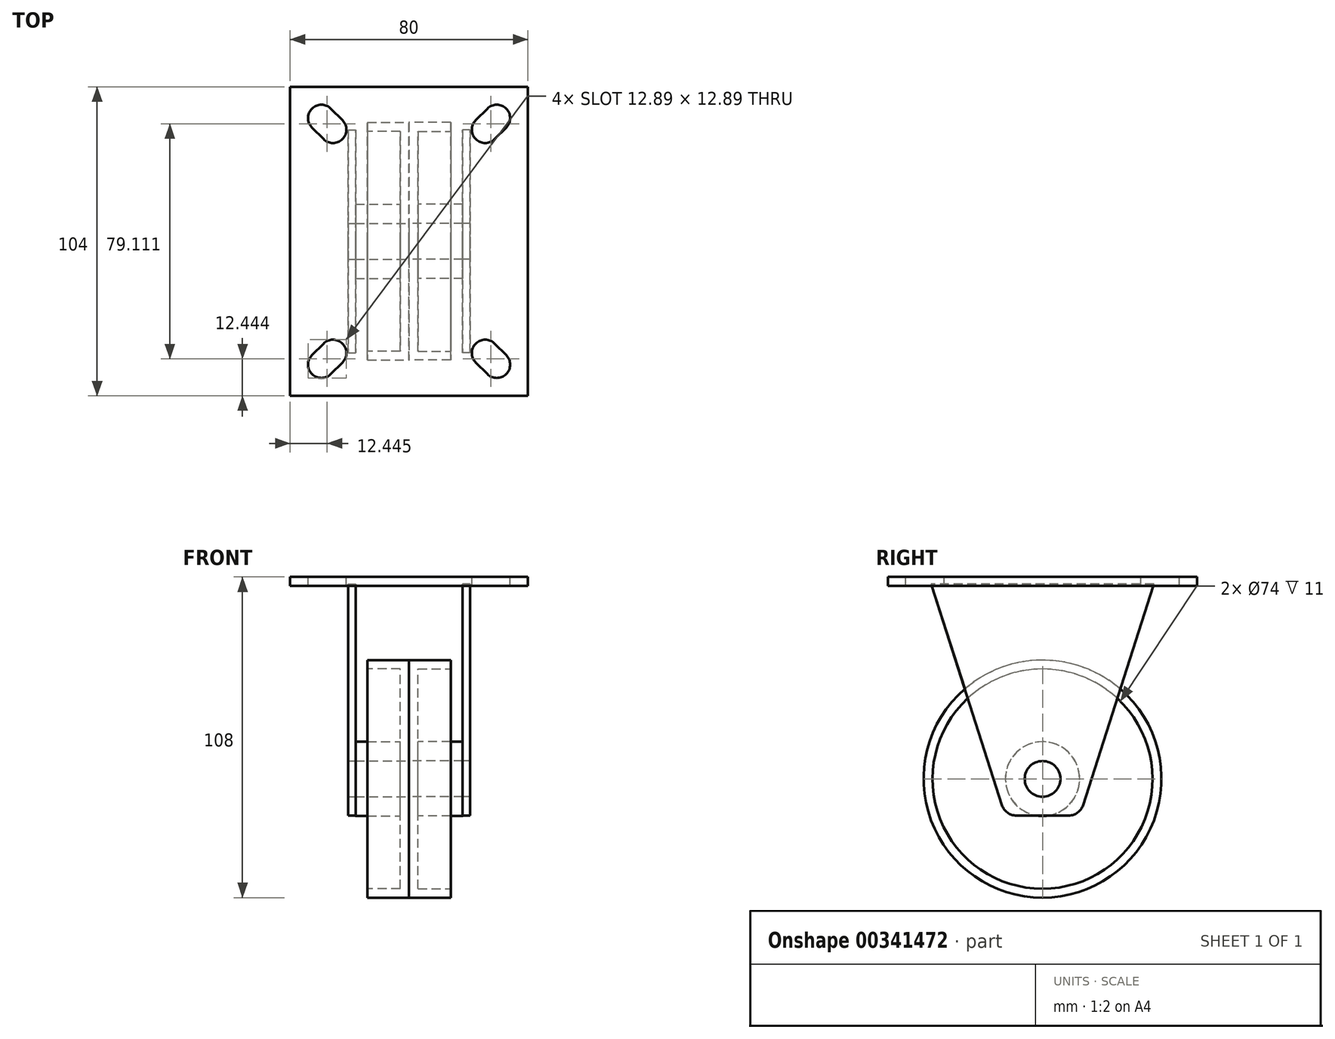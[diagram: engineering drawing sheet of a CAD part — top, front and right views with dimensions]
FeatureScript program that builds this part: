
annotation { "Feature Type Name" : "Feature", "Feature Type Description" : "" }
export const myFeature = defineFeature(function(context is Context, id is Id, definition is map)
    precondition{}
    {
        {
            var Q0;
            Q0=qCreatedBy(makeId("Front.planeOp"),FACE);
            var sketch = newSketch(context, id + "F0", { "sketchPlane" : qUnion([Q0])});
            skLineSegment(sketch, "E0.bottom", {"start": v(-49.77, 0) * mm, "end": v(53.7, 0) * mm, "construction": true});
            skLineSegment(sketch, "E0.top", {"start": v(-49.77, -108) * mm, "end": v(53.7, -108) * mm, "construction": true});
            skLineSegment(sketch, "E0.left", {"start": v(-49.77, 0) * mm, "end": v(-49.77, -108) * mm, "construction": true});
            skLineSegment(sketch, "E0.right", {"start": v(53.7, 0) * mm, "end": v(53.7, -108) * mm, "construction": true});
            skSolve(sketch);
        }
        {
            var Q0;
            Q0=qCreatedBy(makeId("Top.planeOp"),FACE);
            var sketch = newSketch(context, id + "F1", { "sketchPlane" : qUnion([Q0])});
            skLineSegment(sketch, "E1.bottom", {"start": v(-40, 52) * mm, "end": v(40, 52) * mm});
            skLineSegment(sketch, "E1.top", {"start": v(-40, -52) * mm, "end": v(40, -52) * mm});
            skLineSegment(sketch, "E1.left", {"start": v(-40, 52) * mm, "end": v(-40, -52) * mm});
            skLineSegment(sketch, "E1.right", {"start": v(40, 52) * mm, "end": v(40, -52) * mm});
            skLineSegment(sketch, "E2", {"start": v(0, 52) * mm, "end": v(0, -52) * mm, "construction": true});
            skLineSegment(sketch, "E3", {"start": v(-40, 0) * mm, "end": v(0, 0) * mm, "construction": true});
            skLineSegment(sketch, "E4", {"start": v(0, 0) * mm, "end": v(40, 0) * mm, "construction": true});
            skArc(sketch, "E5", {"start": v(-26.32, 44.68) * mm, "mid": v(-32.68, 44.68) * mm, "end": v(-32.68, 38.32) * mm});
            skLineSegment(sketch, "E6", {"start": v(-29.5, 41.5) * mm, "end": v(-26.32, 44.68) * mm, "construction": true});
            skLineSegment(sketch, "E7", {"start": v(-26.32, 44.68) * mm, "end": v(-22.43, 40.8) * mm});
            skLineSegment(sketch, "E8", {"start": v(-22.43, 40.8) * mm, "end": v(-28.8, 34.43) * mm, "construction": true});
            skLineSegment(sketch, "E9", {"start": v(-28.8, 34.43) * mm, "end": v(-32.68, 38.32) * mm});
            skLineSegment(sketch, "E10", {"start": v(-32.68, 38.32) * mm, "end": v(-29.5, 41.5) * mm, "construction": true});
            skLineSegment(sketch, "E11", {"start": v(-29.5, 41.5) * mm, "end": v(-25, 41.5) * mm, "construction": true});
            skArc(sketch, "E12", {"start": v(-28.8, 34.43) * mm, "mid": v(-22.43, 34.43) * mm, "end": v(-22.43, 40.8) * mm});
            skLineSegment(sketch, "E13.MirrorCS", {"start": v(28.8, 34.43) * mm, "end": v(32.68, 38.32) * mm});
            skArc(sketch, "E14.MirrorCS", {"start": v(26.32, 44.68) * mm, "mid": v(32.68, 44.68) * mm, "end": v(32.68, 38.32) * mm});
            skLineSegment(sketch, "E15.MirrorCS", {"start": v(26.32, 44.68) * mm, "end": v(22.43, 40.8) * mm});
            skArc(sketch, "E16.MirrorCS", {"start": v(28.8, 34.43) * mm, "mid": v(22.43, 34.43) * mm, "end": v(22.43, 40.8) * mm});
            skLineSegment(sketch, "E17.MirrorCS", {"start": v(-28.8, -34.43) * mm, "end": v(-32.68, -38.32) * mm});
            skArc(sketch, "E18.MirrorCS", {"start": v(-28.8, -34.43) * mm, "mid": v(-22.43, -34.43) * mm, "end": v(-22.43, -40.8) * mm});
            skLineSegment(sketch, "E19.MirrorCS", {"start": v(-26.32, -44.68) * mm, "end": v(-22.43, -40.8) * mm});
            skArc(sketch, "E20.MirrorCS", {"start": v(-26.32, -44.68) * mm, "mid": v(-32.68, -44.68) * mm, "end": v(-32.68, -38.32) * mm});
            skArc(sketch, "E21.MirrorCS", {"start": v(26.32, -44.68) * mm, "mid": v(32.68, -44.68) * mm, "end": v(32.68, -38.32) * mm});
            skArc(sketch, "E22.MirrorCS", {"start": v(28.8, -34.43) * mm, "mid": v(22.43, -34.43) * mm, "end": v(22.43, -40.8) * mm});
            skLineSegment(sketch, "E23.MirrorCS", {"start": v(26.32, -44.68) * mm, "end": v(22.43, -40.8) * mm});
            skLineSegment(sketch, "E24.MirrorCS", {"start": v(28.8, -34.43) * mm, "end": v(32.68, -38.32) * mm});
            skLineSegment(sketch, "E25", {"start": v(-30.74, 36.37) * mm, "end": v(-24.37, 42.74) * mm, "construction": true});
            skLineSegment(sketch, "E26", {"start": v(-25.61, 37.61) * mm, "end": v(-29.5, 41.5) * mm, "construction": true});
            skLineSegment(sketch, "E27", {"start": v(-27.56, 39.56) * mm, "end": v(0, 39.56) * mm, "construction": true});
            skLineSegment(sketch, "E28", {"start": v(-27.56, 39.56) * mm, "end": v(-27.56, 52) * mm, "construction": true});
            skLineSegment(sketch, "E29", {"start": v(-27.56, 39.56) * mm, "end": v(-27.56, 0) * mm, "construction": true});
            skSolve(sketch);
        }
        {
            var Q0;
            Q0=makeQuery(id+"F1.imprint","IMPRINT",FACE,{"disambiguationData":[TD([[makeQuery(id+"F1.imprint","IMPRINT",EDGE,{"derivedFrom":sQuery(id+"F1.wireOp",EDGE,"E1.bottom")}),-1.0]])]});
            extrude(context, id + "F2", {"entities" : qUnion([Q0]), "oppositeDirection" : true, "depth" : 3 * mm});
        }
        {
            var Q0;
            Q0=qCreatedBy(makeId("Right.planeOp"),FACE);
            var sketch = newSketch(context, id + "F3", { "sketchPlane" : qUnion([Q0])});
            skCircle(sketch, "E30", {"center": v(0, -68) * mm, "radius": 40 * mm});
            skLineSegment(sketch, "E31", {"start": v(17.4, -108) * mm, "end": v(-52.03, -108) * mm, "construction": true});
            skCircle(sketch, "E32", {"center": v(0, -68) * mm, "radius": 6 * mm});
            skCircle(sketch, "E33", {"center": v(0, -68) * mm, "radius": 12.5 * mm});
            skSolve(sketch);
        }
        {
            var Q0;
            Q0=makeQuery(id+"F3.imprint","IMPRINT",FACE,{"disambiguationData":[TD([[makeQuery(id+"F3.imprint","IMPRINT",EDGE,{"derivedFrom":sQuery(id+"F3.wireOp",EDGE,"E30")}),1.0]])]});
            extrude(context, id + "F4", {"entities" : qUnion([Q0]), "depth" : 28 / 2 * mm});
        }
        {
            var Q0;
            Q0=makeQuery(id+"F4.opExtrude","CAP_FACE",FACE,{"disambiguationData":[OSD([sQuery(id+"F3.wireOp",EDGE,"E30")])],"isStart":false});
            var sketch = newSketch(context, id + "F5", { "sketchPlane" : qUnion([Q0])});
            skCircle(sketch, "E34", {"center": v(0, -68) * mm, "radius": 37 * mm});
            skSolve(sketch);
        }
        {
            var Q0;
            Q0=makeQuery(id+"F5.imprint","IMPRINT",FACE,{"disambiguationData":[TD([[makeQuery(id+"F5.imprint","IMPRINT",EDGE,{"derivedFrom":sQuery(id+"F5.wireOp",EDGE,"E34")}),1.0]])]});
            extrude(context, id + "F6", {"entities" : qUnion([Q0]), "operationType" : NewBodyOperationType.REMOVE, "oppositeDirection" : true, "depth" : (28 / 2 - 3) * mm});
        }
        {
            var Q0;
            Q0=makeQuery(id+"F3.imprint","IMPRINT",FACE,{"disambiguationData":[TD([[makeQuery(id+"F3.imprint","IMPRINT",EDGE,{"derivedFrom":sQuery(id+"F3.wireOp",EDGE,"E32")}),-1.0]])]});
            extrude(context, id + "F7", {"entities" : qUnion([Q0]), "operationType" : NewBodyOperationType.ADD, "depth" : 36 / 2 * mm});
        }
        {
            var Q0;
            Q0=makeQuery(id+"F4.opExtrude","SWEPT_BODY",BODY,{"disambiguationData":[OSD([sQuery(id+"F3.wireOp",EDGE,"E30")])]});
            var Q1;
            Q1=qCreatedBy(makeId("Right.planeOp"),FACE);
            mirror(context, id + "F8", {"operationType" : NewBodyOperationType.ADD, "entities" : qUnion([Q0]), "mirrorPlane" : qUnion([Q1])});
        }
        {
            var Q0;
            Q0=makeQuery(id+"F7.opExtrude","CAP_FACE",FACE,{"disambiguationData":[OSD([sQuery(id+"F3.wireOp",EDGE,"E32"),sQuery(id+"F3.wireOp",EDGE,"E33")])],"isStart":false});
            var sketch = newSketch(context, id + "F9", { "sketchPlane" : qUnion([Q0])});
            skLineSegment(sketch, "E35", {"start": v(-8.85, -80.35) * mm, "end": v(8.85, -80.35) * mm});
            skLineSegment(sketch, "E36", {"start": v(13.61, -76.88) * mm, "end": v(37.5, -2.4) * mm});
            skLineSegment(sketch, "E37", {"start": v(37.5, -2.4) * mm, "end": v(-37.5, -2.4) * mm});
            skLineSegment(sketch, "E38", {"start": v(-37.5, -2.4) * mm, "end": v(-13.61, -76.88) * mm});
            skPoint(sketch, "E39.visualSharp", {"position": v(-12.5, -80.35) * mm});
            skArc(sketch, "E39.filletArc", {"start": v(-13.61, -76.88) * mm, "mid": v(-11.8, -79.4) * mm, "end": v(-8.85, -80.35) * mm});
            skPoint(sketch, "E40.visualSharp", {"position": v(12.5, -80.35) * mm});
            skArc(sketch, "E40.filletArc", {"start": v(8.85, -80.35) * mm, "mid": v(11.8, -79.4) * mm, "end": v(13.61, -76.88) * mm});
            skSolve(sketch);
        }
        {
            var Q0;
            Q0=makeQuery(id+"F9.imprint","IMPRINT",FACE,{"disambiguationData":[TD([[makeQuery(id+"F9.imprint","IMPRINT",EDGE,{"derivedFrom":sQuery(id+"F9.wireOp",EDGE,"E35")}),1.0]])]});
            var Q1;
            Q1=makeQuery(id+"F9.imprint","IMPRINT",FACE,{"disambiguationData":[TD([[makeQuery(id+"F9.imprint","IMPRINT",EDGE,{"derivedFrom":makeQuery(id+"F7.opExtrude","CAP_EDGE",EDGE,{"disambiguationData":[OSD([sQuery(id+"F3.wireOp",EDGE,"E32")])],"isStart":false})}),-1.0]])]});
            var Q2;
            Q2=makeQuery(id+"F7.opExtrude","CAP_FACE",FACE,{"disambiguationData":[OSD([sQuery(id+"F3.wireOp",EDGE,"E32"),sQuery(id+"F3.wireOp",EDGE,"E33")])],"isStart":false});
            var Q3;
            Q3=makeQuery(id+"F7.opExtrude","CAP_FACE",FACE,{"disambiguationData":[OSD([sQuery(id+"F3.wireOp",EDGE,"E32"),sQuery(id+"F3.wireOp",EDGE,"E33")])],"isStart":false});
            extrude(context, id + "F10", {"entities" : qUnion([Q0, Q1]), "endBoundEntityFace" : qUnion([Q2]), "depth" : 2.5 * mm});
        }
        {
            var Q0;
            Q0=makeQuery(id+"F10.opExtrude","SWEPT_BODY",BODY,{"disambiguationData":[OSD([sQuery(id+"F3.wireOp",EDGE,"E32"),sQuery(id+"F9.wireOp",EDGE,"E35"),sQuery(id+"F9.wireOp",EDGE,"E36"),sQuery(id+"F9.wireOp",EDGE,"E37"),sQuery(id+"F9.wireOp",EDGE,"E38"),sQuery(id+"F9.wireOp",EDGE,"E39.filletArc"),sQuery(id+"F9.wireOp",EDGE,"E40.filletArc")])]});
            var Q1;
            Q1=qCreatedBy(makeId("Right.planeOp"),FACE);
            mirror(context, id + "F11", {"entities" : qUnion([Q0]), "mirrorPlane" : qUnion([Q1])});
        }
    });
